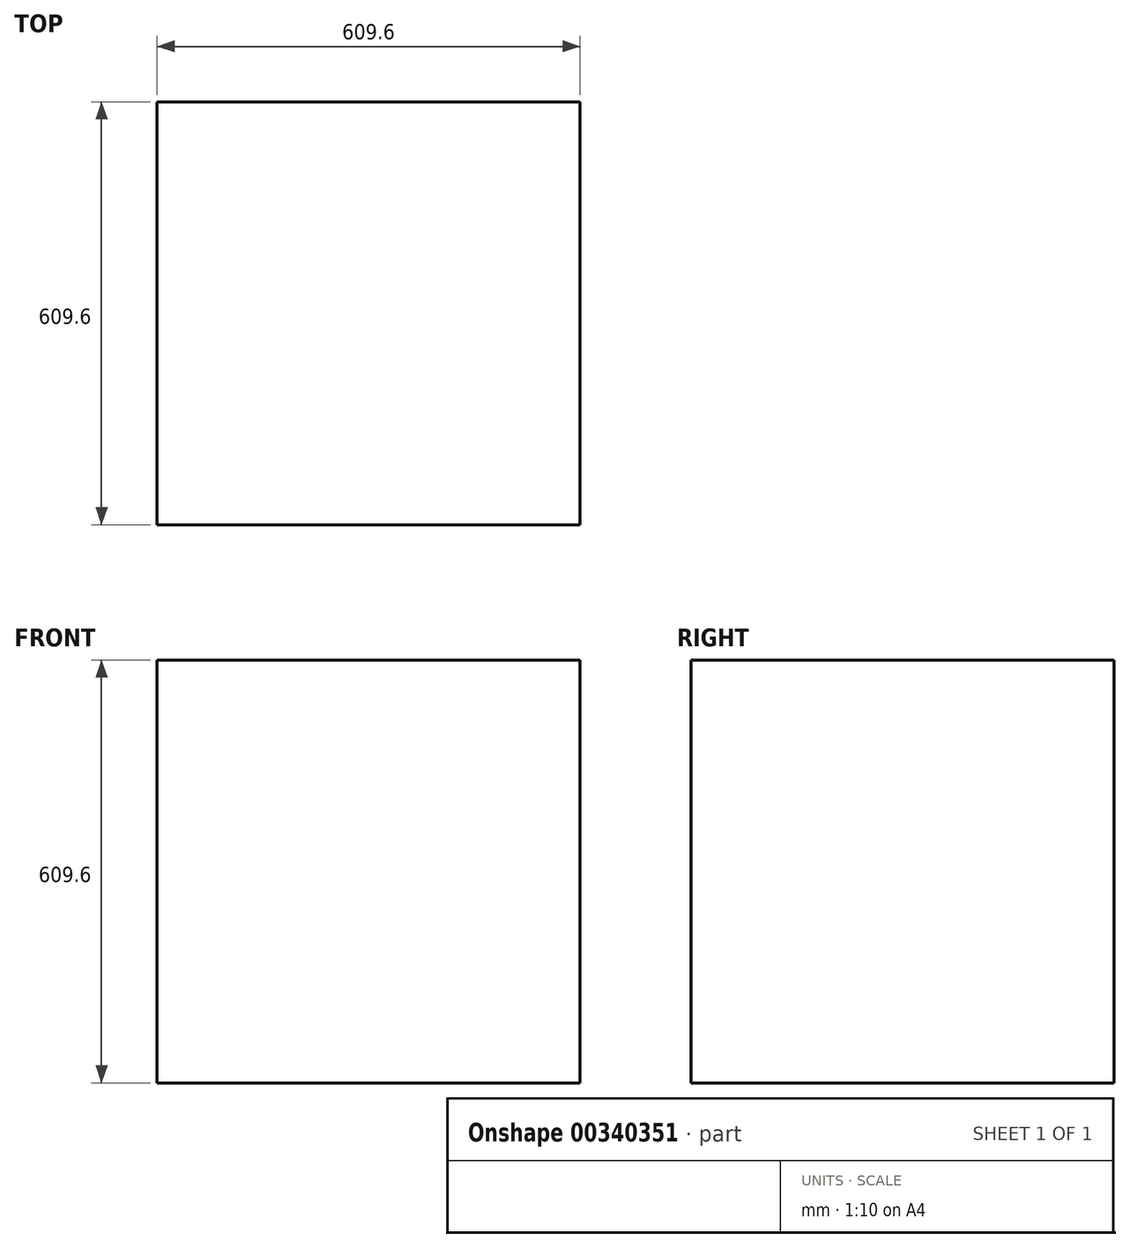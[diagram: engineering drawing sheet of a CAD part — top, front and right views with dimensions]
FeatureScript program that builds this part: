
annotation { "Feature Type Name" : "Feature", "Feature Type Description" : "" }
export const myFeature = defineFeature(function(context is Context, id is Id, definition is map)
    precondition{}
    {
        {
            var Q0;
            Q0=qCreatedBy(makeId("Front.planeOp"),FACE);
            var sketch = newSketch(context, id + "F0", { "sketchPlane" : qUnion([Q0])});
            skLineSegment(sketch, "E0.bottom", {"start": v(-299.2, 319.75) * mm, "end": v(310.4, 319.75) * mm});
            skLineSegment(sketch, "E0.top", {"start": v(-299.2, -289.85) * mm, "end": v(310.4, -289.85) * mm});
            skLineSegment(sketch, "E0.left", {"start": v(-299.2, 319.75) * mm, "end": v(-299.2, -289.85) * mm});
            skLineSegment(sketch, "E0.right", {"start": v(310.4, 319.75) * mm, "end": v(310.4, -289.85) * mm});
            skSolve(sketch);
        }
        {
            var Q0;
            Q0=makeQuery(id+"F0.imprint","IMPRINT",FACE,{"disambiguationData":[TD([[makeQuery(id+"F0.imprint","IMPRINT",EDGE,{"derivedFrom":sQuery(id+"F0.wireOp",EDGE,"E0.bottom")}),-1.0]])]});
            extrude(context, id + "F1", {"entities" : qUnion([Q0]), "depth" : 609.6 * mm});
        }
    });
